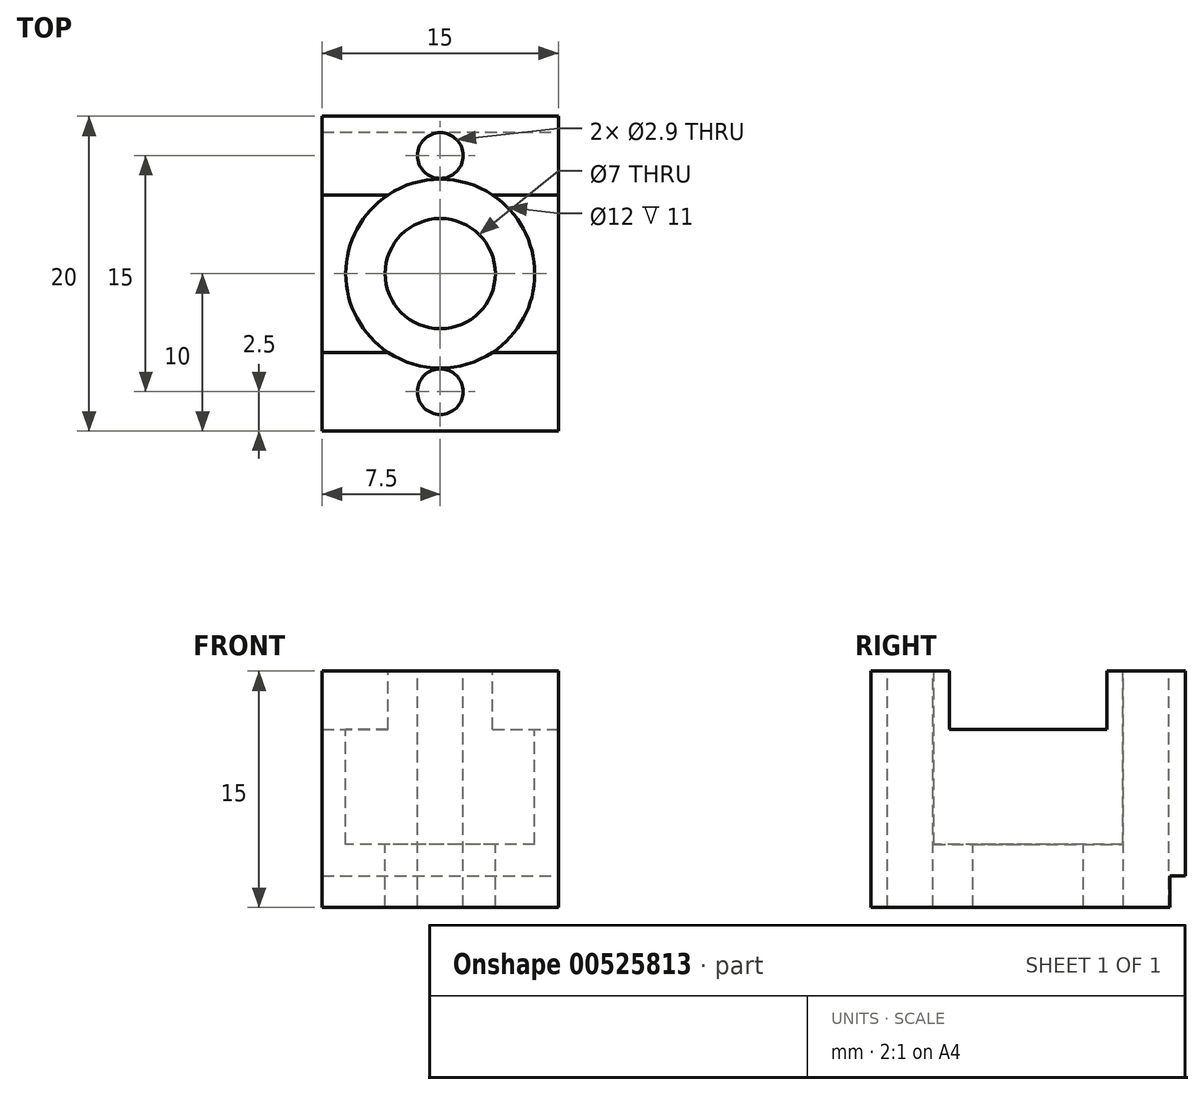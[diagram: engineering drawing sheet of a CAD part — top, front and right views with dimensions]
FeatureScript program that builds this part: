
annotation { "Feature Type Name" : "Feature", "Feature Type Description" : "" }
export const myFeature = defineFeature(function(context is Context, id is Id, definition is map)
    precondition{}
    {
        {
            var Q0;
            Q0=qCreatedBy(makeId("Top.planeOp"),FACE);
            var sketch = newSketch(context, id + "F0", { "sketchPlane" : qUnion([Q0])});
            skLineSegment(sketch, "E0.bottom", {"start": v(7.5, 10) * mm, "end": v(-7.5, 10) * mm});
            skLineSegment(sketch, "E0.top", {"start": v(7.5, -10) * mm, "end": v(-7.5, -10) * mm});
            skLineSegment(sketch, "E0.left", {"start": v(7.5, 10) * mm, "end": v(7.5, -10) * mm});
            skLineSegment(sketch, "E0.right", {"start": v(-7.5, 10) * mm, "end": v(-7.5, -10) * mm});
            skPoint(sketch, "E0.middle", {"position": v(0, 0) * mm});
            skSolve(sketch);
        }
        {
            var Q0;
            Q0=makeQuery(id+"F0.imprint","IMPRINT",FACE,{"disambiguationData":[TD([[makeQuery(id+"F0.imprint","IMPRINT",EDGE,{"derivedFrom":sQuery(id+"F0.wireOp",EDGE,"E0.bottom")}),1.0]])]});
            extrude(context, id + "F1", {"entities" : qUnion([Q0]), "depth" : 15 * mm, "offsetDistance" : 25 * mm});
        }
        {
            var Q0;
            Q0=makeQuery(id+"F1.opExtrude","CAP_FACE",FACE,{"disambiguationData":[OSD([sQuery(id+"F0.wireOp",EDGE,"E0.bottom"),sQuery(id+"F0.wireOp",EDGE,"E0.top"),sQuery(id+"F0.wireOp",EDGE,"E0.left"),sQuery(id+"F0.wireOp",EDGE,"E0.right")])],"isStart":false});
            var sketch = newSketch(context, id + "F2", { "sketchPlane" : qUnion([Q0])});
            skPoint(sketch, "E1", {"position": v(0, 0) * mm});
            skLineSegment(sketch, "E2", {"start": v(-7.5, 0) * mm, "end": v(7.5, 0) * mm, "construction": true});
            skLineSegment(sketch, "E3", {"start": v(0, -10) * mm, "end": v(0, 10) * mm, "construction": true});
            skPoint(sketch, "E4", {"position": v(0, -7.5) * mm});
            skPoint(sketch, "E5", {"position": v(0, 7.5) * mm});
            skSolve(sketch);
        }
        {
            var Q0;
            Q0=sQuery(id+"F2.wireOp",VERTEX,"E1");
            var Q1;
            Q1=makeQuery(id+"F1.opExtrude","SWEPT_BODY",BODY,{"disambiguationData":[OSD([sQuery(id+"F0.wireOp",EDGE,"E0.bottom"),sQuery(id+"F0.wireOp",EDGE,"E0.top"),sQuery(id+"F0.wireOp",EDGE,"E0.left"),sQuery(id+"F0.wireOp",EDGE,"E0.right")])]});
            hole(context, id + "F3", {"style" : HoleStyle.C_BORE, "endStyle" : HoleEndStyle.THROUGH, "holeDiameter" : 7 * mm, "cBoreDiameter" : 12 * mm, "cBoreDepth" : 11 * mm, "isTappedThrough" : true, "tappedDepth" : 12 * mm, "tapClearance" : 3, "startFromSketch" : true, "locations" : qUnion([Q0]), "scope" : qUnion([Q1])});
        }
        {
            var Q0;
            Q0=sQuery(id+"F2.wireOp",VERTEX,"E4");
            var Q1;
            Q1=sQuery(id+"F2.wireOp",VERTEX,"E5");
            var Q2;
            Q2=makeQuery(id+"F1.opExtrude","SWEPT_BODY",BODY,{"disambiguationData":[OSD([sQuery(id+"F0.wireOp",EDGE,"E0.bottom"),sQuery(id+"F0.wireOp",EDGE,"E0.top"),sQuery(id+"F0.wireOp",EDGE,"E0.left"),sQuery(id+"F0.wireOp",EDGE,"E0.right")])]});
            hole(context, id + "F4", {"style" : HoleStyle.SIMPLE, "endStyle" : HoleEndStyle.THROUGH, "holeDiameter" : 2.9 * mm, "isTappedThrough" : true, "tappedDepth" : 12 * mm, "tapClearance" : 3, "startFromSketch" : true, "locations" : qUnion([Q0, Q1]), "scope" : qUnion([Q2])});
        }
        {
            var Q0;
            Q0=makeQuery(id+"F1.opExtrude","SWEPT_FACE",FACE,{"disambiguationData":[OSD([sQuery(id+"F0.wireOp",EDGE,"E0.left")])]});
            var sketch = newSketch(context, id + "F5", { "sketchPlane" : qUnion([Q0])});
            skLineSegment(sketch, "E6", {"start": v(0, 15) * mm, "end": v(0, 0) * mm, "construction": true});
            skLineSegment(sketch, "E7.bottom", {"start": v(-5, 15) * mm, "end": v(5, 15) * mm});
            skLineSegment(sketch, "E7.top", {"start": v(-5, 11.3) * mm, "end": v(5, 11.3) * mm});
            skLineSegment(sketch, "E7.left", {"start": v(-5, 15) * mm, "end": v(-5, 11.3) * mm});
            skLineSegment(sketch, "E7.right", {"start": v(5, 15) * mm, "end": v(5, 11.3) * mm});
            skSolve(sketch);
        }
        {
            var Q0;
            Q0=makeQuery(id+"F5.imprint","IMPRINT",FACE,{"disambiguationData":[TD([[makeQuery(id+"F5.imprint","IMPRINT",EDGE,{"derivedFrom":sQuery(id+"F5.wireOp",EDGE,"E7.bottom")}),1.0]])]});
            extrude(context, id + "F6", {"entities" : qUnion([Q0]), "operationType" : NewBodyOperationType.REMOVE, "endBound" : BoundingType.THROUGH_ALL, "oppositeDirection" : true, "depth" : 25 * mm, "offsetDistance" : 25 * mm});
        }
        {
            var Q0;
            Q0=makeQuery(id+"F1.opExtrude","SWEPT_FACE",FACE,{"disambiguationData":[OSD([sQuery(id+"F0.wireOp",EDGE,"E0.left")])]});
            var sketch = newSketch(context, id + "F7", { "sketchPlane" : qUnion([Q0])});
            skLineSegment(sketch, "E8.bottom", {"start": v(10, 0) * mm, "end": v(9, 0) * mm});
            skLineSegment(sketch, "E8.top", {"start": v(10, 2) * mm, "end": v(9, 2) * mm});
            skLineSegment(sketch, "E8.left", {"start": v(10, 0) * mm, "end": v(10, 2) * mm});
            skLineSegment(sketch, "E8.right", {"start": v(9, 0) * mm, "end": v(9, 2) * mm});
            skSolve(sketch);
        }
        {
            var Q0;
            Q0=makeQuery(id+"F7.imprint","IMPRINT",FACE,{"disambiguationData":[TD([[makeQuery(id+"F7.imprint","IMPRINT",EDGE,{"derivedFrom":sQuery(id+"F7.wireOp",EDGE,"E8.bottom")}),-1.0]])]});
            extrude(context, id + "F8", {"entities" : qUnion([Q0]), "operationType" : NewBodyOperationType.REMOVE, "endBound" : BoundingType.THROUGH_ALL, "oppositeDirection" : true, "depth" : 25 * mm, "offsetDistance" : 25 * mm});
        }
    });
